# Revit family: Deca_Saboneteira Flex_2010.C.FLX_Parede
name_source: partatom
category: Plumbing Fixtures
revit_build: Autodesk Revit Architecture 2012 (Build: 20120126_0600(x64)
units: mm (PartAtom-declared; Revit-internal decimal feet)

## types (1)
- 2010.C.FLX_Cromado CR10
    Aprovado por = Contino/quattroD
    Assembly Code = D2010
    Atendimento ao Cliente = 0800-0117073
    Criado por = Contino/quattroD
    Código = 2010.C.FLX
    Default Elevation = 800 mm  [stored 2.62467 ft]
    Description = Saboneteira de parede
    HWFU = 0
    Informações Complementares = Os parafusos e buchas que acompanham o produto devem ser utilzados apenas em paredes de concreto ou tijolo maciço. Para instalações em Drywall, consultar projetista ou engenheiro da obra.
    Linha = Flex
    Louça/Metais = Metal
    Manufacturer = Deca
    Material = Deca_Latão Cromado e Plástico de Engenharia
    Model = 2010.C.FLX
    Norma = ABNT NBR 10283: 2003
    Peso Liquido (Kg) = 0.24
    Produto = Saboneteira de parede Flex
    Saboneteira = Deca CR10 Cromado
    Segmento = Competitivo
    URL = www.deca.com.br/produtos
    Variações de COR = Cromado (2010.C.FLX)

note: [stored X ft] marks values corroborated as IEEE doubles in the binary element streams (Revit-internal decimal feet)

## geometry (parser evidence)
native form markers: Blend x4, Sweep x2
no freeform markers — native parametric forms only
